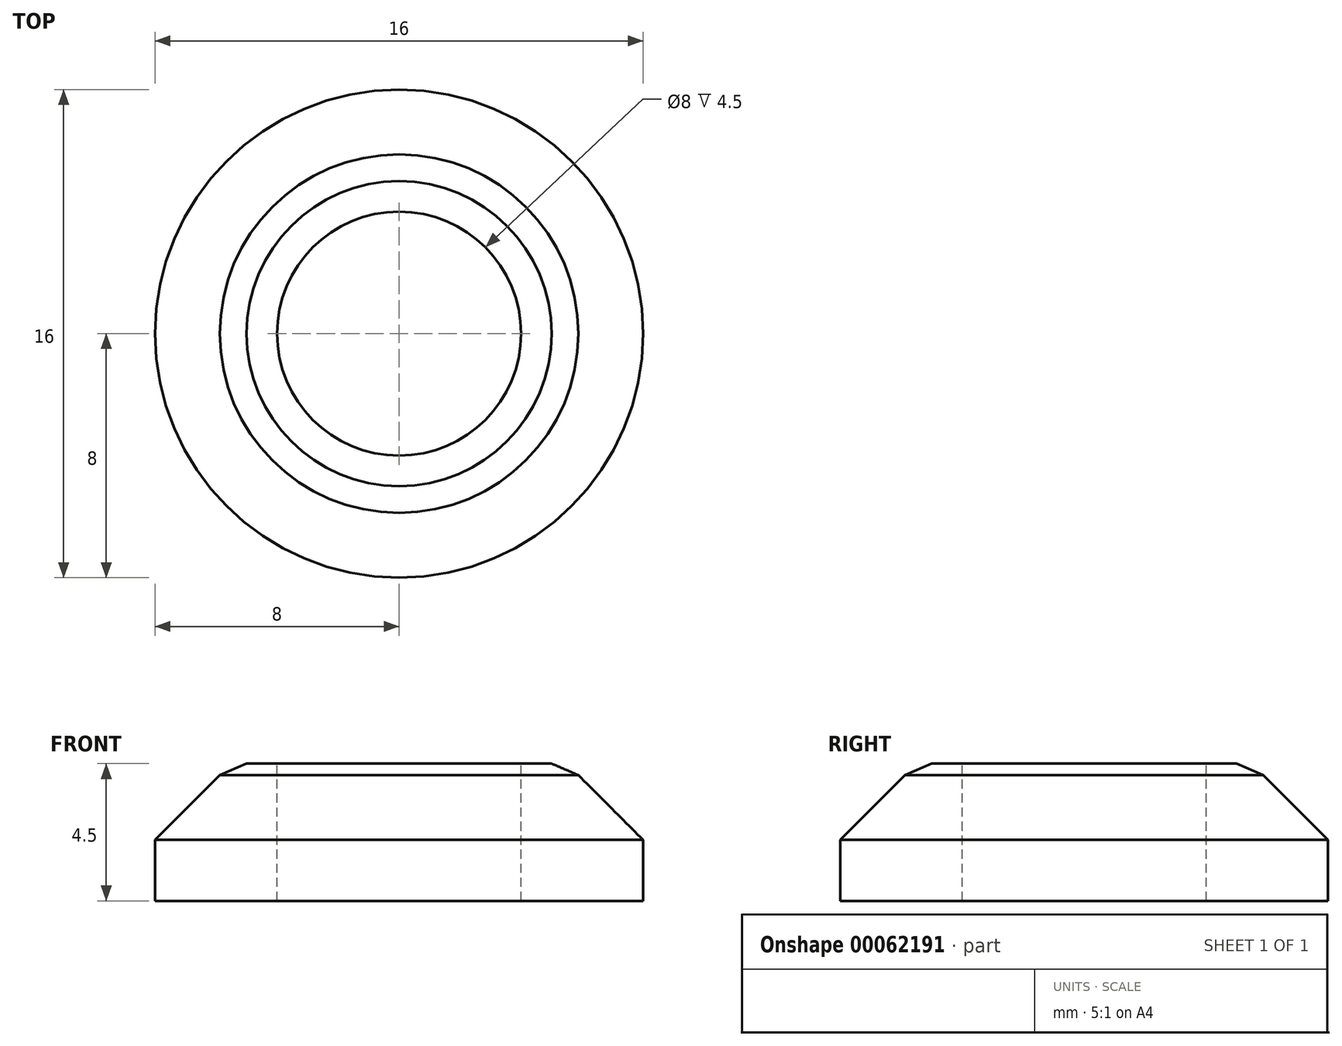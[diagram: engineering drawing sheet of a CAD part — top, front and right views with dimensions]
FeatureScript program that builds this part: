
annotation { "Feature Type Name" : "Feature", "Feature Type Description" : "" }
export const myFeature = defineFeature(function(context is Context, id is Id, definition is map)
    precondition{}
    {
        {
            var Q0;
            Q0=qCreatedBy(makeId("Front.planeOp"),FACE);
            var sketch = newSketch(context, id + "F0", { "sketchPlane" : qUnion([Q0])});
            skLineSegment(sketch, "E0", {"start": v(4, 0) * mm, "end": v(8, 0) * mm});
            skLineSegment(sketch, "E1", {"start": v(8, 0) * mm, "end": v(8, 2) * mm});
            skLineSegment(sketch, "E2", {"start": v(8, 2) * mm, "end": v(5.88, 4.12) * mm});
            skLineSegment(sketch, "E3", {"start": v(5.88, 4.12) * mm, "end": v(5, 4.5) * mm});
            skLineSegment(sketch, "E4", {"start": v(4, 4.5) * mm, "end": v(4, 0) * mm});
            skLineSegment(sketch, "E5", {"start": v(0, 13.54) * mm, "end": v(0, -3.67) * mm, "construction": true});
            skLineSegment(sketch, "E6", {"start": v(5, 4.5) * mm, "end": v(4, 4.5) * mm});
            skSolve(sketch);
        }
        {
            var Q0;
            Q0=makeQuery(id+"F0.imprint","IMPRINT",FACE,{"disambiguationData":[TD([[makeQuery(id+"F0.imprint","IMPRINT",EDGE,{"derivedFrom":sQuery(id+"F0.wireOp",EDGE,"E0")}),1.0]])]});
            var Q1;
            Q1=sQuery(id+"F0.wireOp",EDGE,"E5");
            revolve(context, id + "F1", {"entities" : qUnion([Q0]), "axis" : qUnion([Q1]), "revolveType" : RevolveType.FULL});
        }
    });
